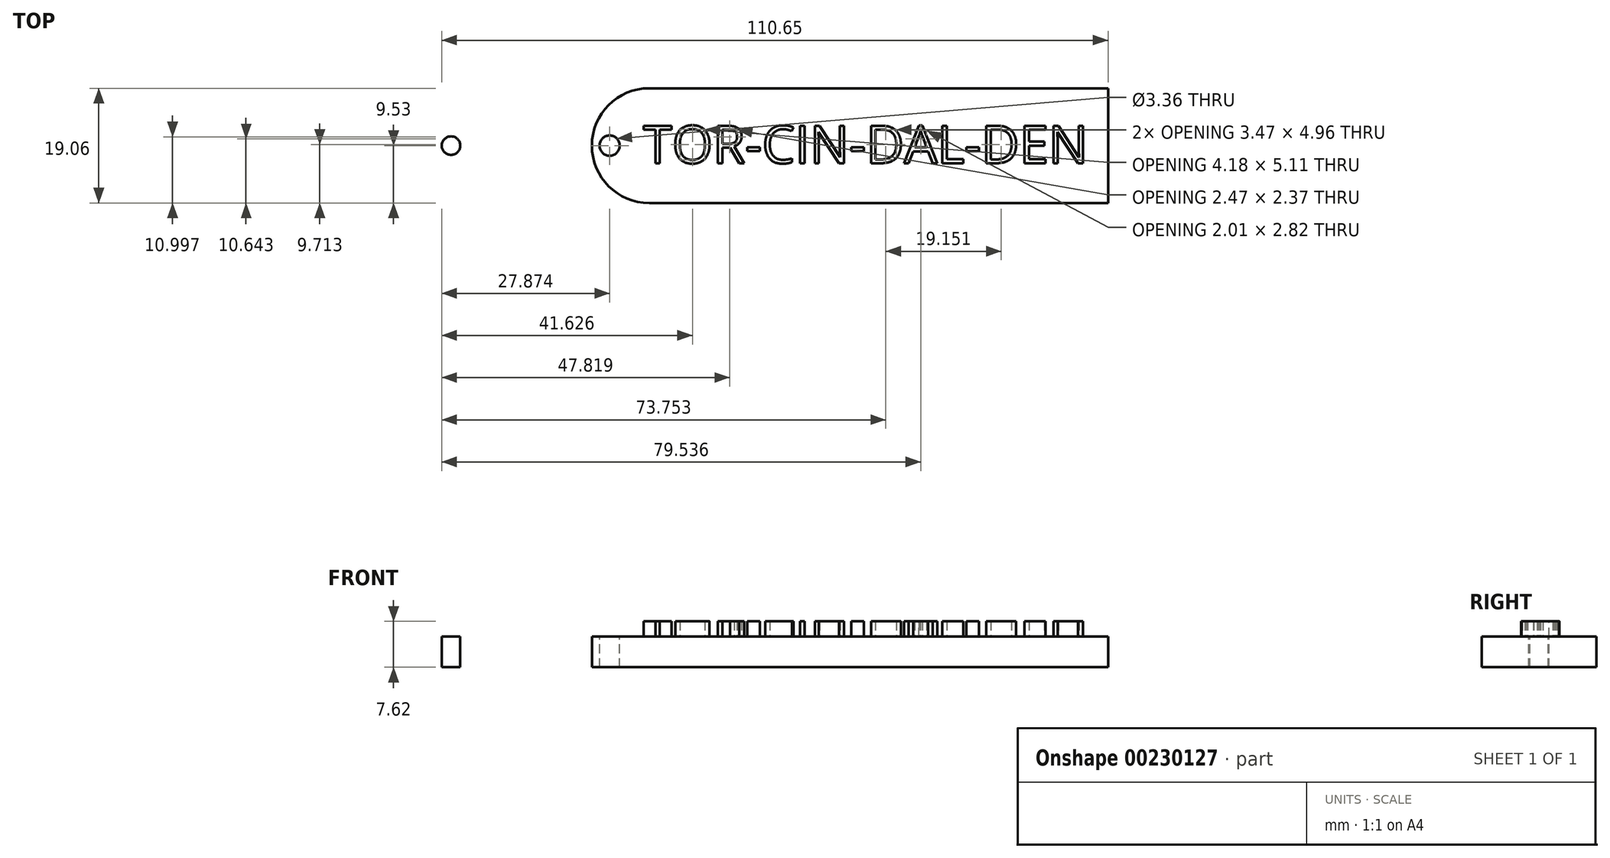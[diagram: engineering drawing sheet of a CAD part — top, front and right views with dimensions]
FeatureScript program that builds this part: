
annotation { "Feature Type Name" : "Feature", "Feature Type Description" : "" }
export const myFeature = defineFeature(function(context is Context, id is Id, definition is map)
    precondition{}
    {
        {
            var Q0;
            Q0=qCreatedBy(makeId("Top.planeOp"),FACE);
            var sketch = newSketch(context, id + "F0", { "sketchPlane" : qUnion([Q0])});
            skLineSegment(sketch, "E0.bottom", {"start": v(55.22, 9.53) * mm, "end": v(-20.98, 9.53) * mm});
            skLineSegment(sketch, "E0.top", {"start": v(55.22, -9.53) * mm, "end": v(-20.98, -9.52) * mm});
            skLineSegment(sketch, "E0.left", {"start": v(55.22, 9.53) * mm, "end": v(55.22, -9.53) * mm});
            skLineSegment(sketch, "E0.right", {"start": v(-20.98, 9.52) * mm, "end": v(-20.98, -9.52) * mm});
            skArc(sketch, "E1", {"start": v(-20.98, 9.53) * mm, "mid": v(-30.5, 0) * mm, "end": v(-20.98, -9.52) * mm});
            skLineSegment(sketch, "E2", {"start": v(-20.98, 0) * mm, "end": v(-30.5, 0) * mm});
            skCircle(sketch, "E3", {"center": v(-53.9, 0) * mm, "radius": 1.54 * mm});
            skCircle(sketch, "E4", {"center": v(-27.56, 0) * mm, "radius": 1.68 * mm});
            skSolve(sketch);
        }
        {
            var Q0;
            Q0=qCreatedBy(makeId("Top.planeOp"),FACE);
            var sketch = newSketch(context, id + "F1", { "sketchPlane" : qUnion([Q0])});
            skText(sketch, "E5", { "text": "TOR-CIN-DAL-DEN", "fontName": "OpenSans-Regular.ttf"});
            const initialGuessF1  = {"E5": [-0.022, -0.00292, 1, 0, 0.00626]};
            skSetInitialGuess(sketch, initialGuessF1);
            skSolve(sketch);
        }
        {
            var Q0;
            Q0 = qSketchRegion(id + "F1", true);
            extrude(context, id + "F2", {"entities" : qUnion([Q0]), "depth" : 2.54 * mm});
        }
        {
            var Q0;
            Q0 = qSketchRegion(id + "F0", true);
            extrude(context, id + "F3", {"entities" : qUnion([Q0]), "oppositeDirection" : true, "depth" : 5.08 * mm});
        }
    });
